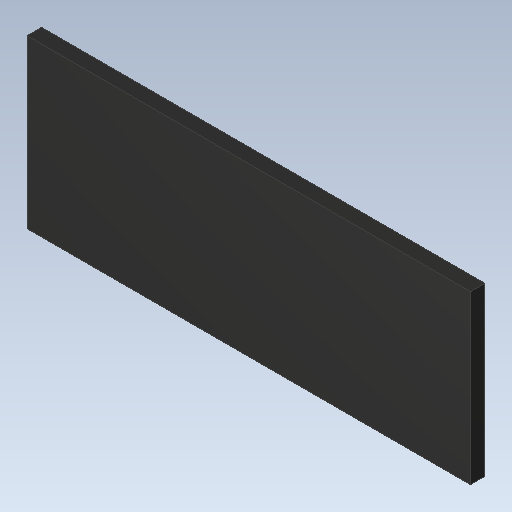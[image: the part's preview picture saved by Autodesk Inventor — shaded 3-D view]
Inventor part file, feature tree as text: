
AUTODESK INVENTOR PART (.ipt)
format: ipt  version: 2023 (Build 270158000, 158)  size: 91,136 bytes
history: imported  units: in
note: dims shown in document units (in); Inventor stores cm internally (conversion verified against a paired STEP export)
features: imported_body x1
ambient origin geometry x8: Origin, YZ Plane, XZ Plane, XY Plane, X Axis, Y Axis, Z Axis, Center Point
bodies: Solid1 (imported_parasolid), Body1 (imported_parasolid)
feature tree (1):
  imported_body  NMx_Import_Brep_tag  [imported B-rep: ~6 faces, bbox_mm=[3.0661, 1.1557, 0.1]]
